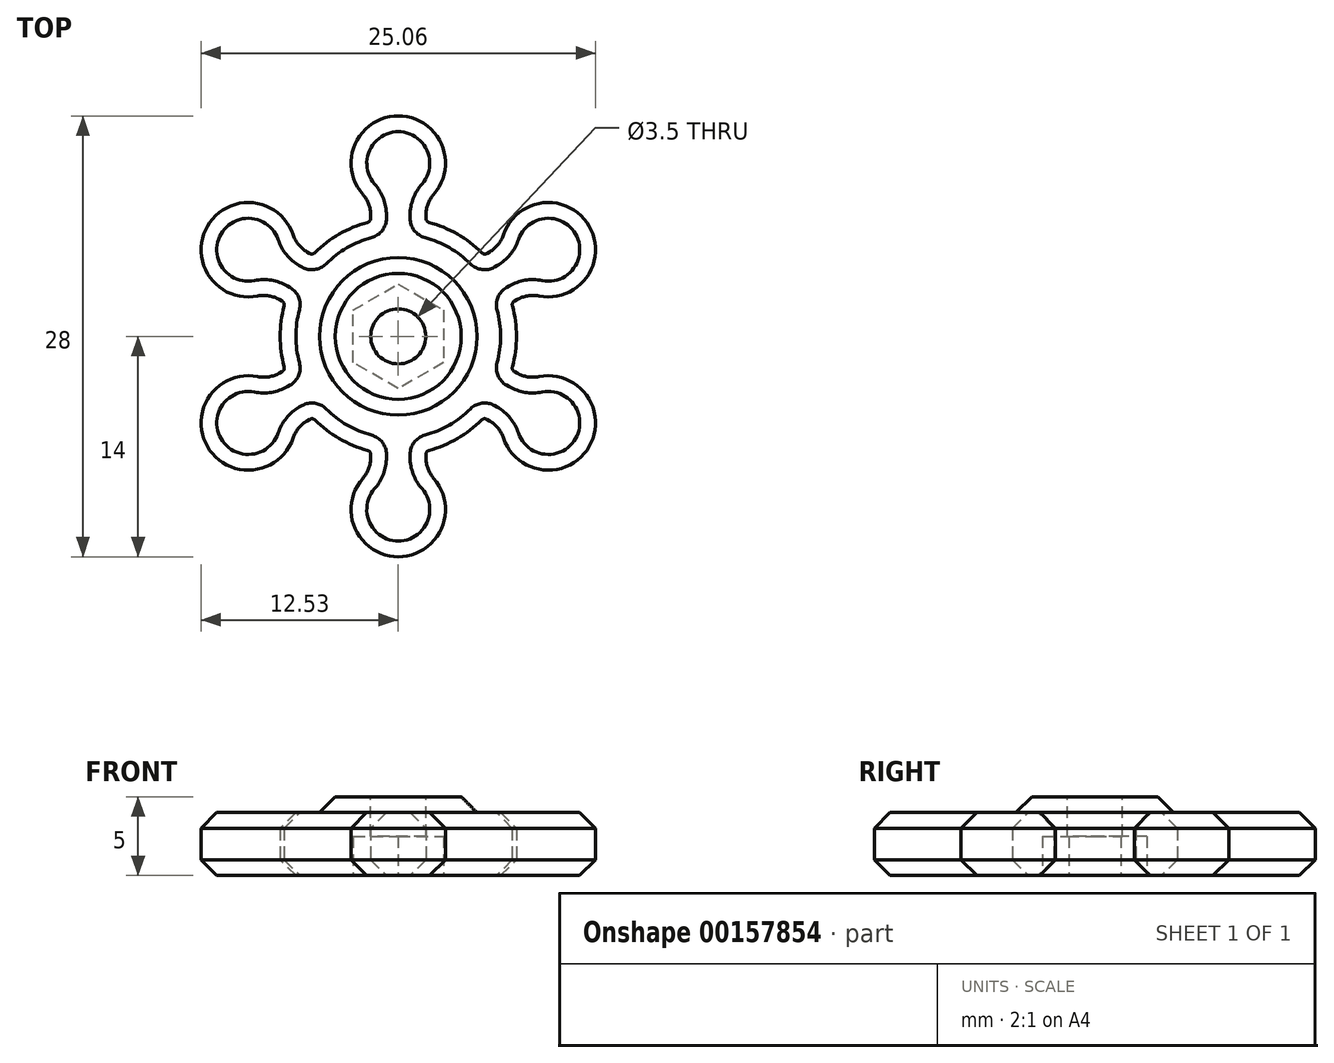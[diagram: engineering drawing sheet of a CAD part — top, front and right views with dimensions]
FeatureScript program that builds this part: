
annotation { "Feature Type Name" : "Feature", "Feature Type Description" : "" }
export const myFeature = defineFeature(function(context is Context, id is Id, definition is map)
    precondition{}
    {
        {
            var Q0;
            Q0=qCreatedBy(makeId("Top.planeOp"),FACE);
            var sketch = newSketch(context, id + "F0", { "sketchPlane" : qUnion([Q0])});
            skArc(sketch, "E0", {"start": v(-1.95, 7.24) * mm, "mid": v(-3.75, 6.5) * mm, "end": v(-5.3, 5.31) * mm});
            skArc(sketch, "E1", {"start": v(2.25, 9.02) * mm, "mid": v(0, 14) * mm, "end": v(-2.25, 9.02) * mm});
            skLineSegment(sketch, "E2.left", {"start": v(-1.75, 7.5) * mm, "end": v(-1.75, 7.7) * mm});
            skLineSegment(sketch, "E2.right", {"start": v(1.75, 7.5) * mm, "end": v(1.75, 7.7) * mm});
            skPoint(sketch, "E3.orphan", {"position": v(-1.75, 0) * mm});
            skPoint(sketch, "E4.visualSharp", {"position": v(-1.75, 8.56) * mm});
            skArc(sketch, "E4.filletArc", {"start": v(-1.75, 7.7) * mm, "mid": v(-1.88, 8.4) * mm, "end": v(-2.25, 9.02) * mm});
            skPoint(sketch, "E5.visualSharp", {"position": v(1.75, 8.56) * mm});
            skArc(sketch, "E5.filletArc", {"start": v(2.25, 9.02) * mm, "mid": v(1.88, 8.4) * mm, "end": v(1.75, 7.7) * mm});
            skPoint(sketch, "E6.visualSharp", {"position": v(1.75, 7.3) * mm});
            skArc(sketch, "E6.filletArc", {"start": v(1.75, 7.5) * mm, "mid": v(1.8, 7.34) * mm, "end": v(1.95, 7.24) * mm});
            skPoint(sketch, "E7.visualSharp", {"position": v(-1.75, 7.3) * mm});
            skArc(sketch, "E7.filletArc", {"start": v(-1.95, 7.24) * mm, "mid": v(-1.8, 7.34) * mm, "end": v(-1.75, 7.5) * mm});
            skArc(sketch, "E8.1.0", {"start": v(-6.68, 6.46) * mm, "mid": v(-12.12, 7) * mm, "end": v(-8.93, 2.56) * mm});
            skArc(sketch, "E8.1.1", {"start": v(-6.68, 6.46) * mm, "mid": v(-6.33, 5.83) * mm, "end": v(-5.79, 5.36) * mm});
            skArc(sketch, "E8.1.2", {"start": v(-7.54, 2.33) * mm, "mid": v(-8.21, 2.57) * mm, "end": v(-8.93, 2.56) * mm});
            skLineSegment(sketch, "E8.1.3", {"start": v(-7.37, 2.24) * mm, "end": v(-7.54, 2.33) * mm});
            skArc(sketch, "E8.1.4", {"start": v(-7.25, 1.93) * mm, "mid": v(-7.26, 2.1) * mm, "end": v(-7.37, 2.24) * mm});
            skLineSegment(sketch, "E8.1.5", {"start": v(-5.62, 5.27) * mm, "end": v(-5.79, 5.36) * mm});
            skArc(sketch, "E8.1.6", {"start": v(-5.62, 5.27) * mm, "mid": v(-5.45, 5.23) * mm, "end": v(-5.3, 5.31) * mm});
            skArc(sketch, "E8.2.0", {"start": v(-8.93, -2.56) * mm, "mid": v(-12.12, -7) * mm, "end": v(-6.68, -6.46) * mm});
            skArc(sketch, "E8.2.1", {"start": v(-8.93, -2.56) * mm, "mid": v(-8.21, -2.57) * mm, "end": v(-7.54, -2.33) * mm});
            skArc(sketch, "E8.2.2", {"start": v(-5.79, -5.36) * mm, "mid": v(-6.33, -5.83) * mm, "end": v(-6.68, -6.46) * mm});
            skLineSegment(sketch, "E8.2.3", {"start": v(-5.62, -5.27) * mm, "end": v(-5.79, -5.36) * mm});
            skArc(sketch, "E8.2.4", {"start": v(-5.3, -5.31) * mm, "mid": v(-5.45, -5.23) * mm, "end": v(-5.62, -5.27) * mm});
            skLineSegment(sketch, "E8.2.5", {"start": v(-7.37, -2.24) * mm, "end": v(-7.54, -2.33) * mm});
            skArc(sketch, "E8.2.6", {"start": v(-7.37, -2.24) * mm, "mid": v(-7.26, -2.1) * mm, "end": v(-7.25, -1.93) * mm});
            skArc(sketch, "E8.3.0", {"start": v(-2.25, -9.02) * mm, "mid": v(0, -14) * mm, "end": v(2.25, -9.02) * mm});
            skArc(sketch, "E8.3.1", {"start": v(-2.25, -9.02) * mm, "mid": v(-1.88, -8.4) * mm, "end": v(-1.75, -7.7) * mm});
            skArc(sketch, "E8.3.2", {"start": v(1.75, -7.7) * mm, "mid": v(1.88, -8.4) * mm, "end": v(2.25, -9.02) * mm});
            skLineSegment(sketch, "E8.3.3", {"start": v(1.75, -7.5) * mm, "end": v(1.75, -7.7) * mm});
            skArc(sketch, "E8.3.4", {"start": v(1.95, -7.24) * mm, "mid": v(1.8, -7.34) * mm, "end": v(1.75, -7.5) * mm});
            skLineSegment(sketch, "E8.3.5", {"start": v(-1.75, -7.5) * mm, "end": v(-1.75, -7.7) * mm});
            skArc(sketch, "E8.3.6", {"start": v(-1.75, -7.5) * mm, "mid": v(-1.8, -7.34) * mm, "end": v(-1.95, -7.24) * mm});
            skArc(sketch, "E8.4.0", {"start": v(6.68, -6.46) * mm, "mid": v(12.12, -7) * mm, "end": v(8.93, -2.56) * mm});
            skArc(sketch, "E8.4.1", {"start": v(6.68, -6.46) * mm, "mid": v(6.33, -5.83) * mm, "end": v(5.79, -5.36) * mm});
            skArc(sketch, "E8.4.2", {"start": v(7.54, -2.33) * mm, "mid": v(8.21, -2.57) * mm, "end": v(8.93, -2.56) * mm});
            skLineSegment(sketch, "E8.4.3", {"start": v(7.37, -2.24) * mm, "end": v(7.54, -2.33) * mm});
            skArc(sketch, "E8.4.4", {"start": v(7.25, -1.93) * mm, "mid": v(7.26, -2.1) * mm, "end": v(7.37, -2.24) * mm});
            skLineSegment(sketch, "E8.4.5", {"start": v(5.62, -5.27) * mm, "end": v(5.79, -5.36) * mm});
            skArc(sketch, "E8.4.6", {"start": v(5.62, -5.27) * mm, "mid": v(5.45, -5.23) * mm, "end": v(5.3, -5.31) * mm});
            skArc(sketch, "E8.5.0", {"start": v(8.93, 2.56) * mm, "mid": v(12.12, 7) * mm, "end": v(6.68, 6.46) * mm});
            skArc(sketch, "E8.5.1", {"start": v(8.93, 2.56) * mm, "mid": v(8.21, 2.57) * mm, "end": v(7.54, 2.33) * mm});
            skArc(sketch, "E8.5.2", {"start": v(5.79, 5.36) * mm, "mid": v(6.33, 5.83) * mm, "end": v(6.68, 6.46) * mm});
            skLineSegment(sketch, "E8.5.3", {"start": v(5.62, 5.27) * mm, "end": v(5.79, 5.36) * mm});
            skArc(sketch, "E8.5.4", {"start": v(5.3, 5.31) * mm, "mid": v(5.45, 5.23) * mm, "end": v(5.62, 5.27) * mm});
            skLineSegment(sketch, "E8.5.5", {"start": v(7.37, 2.24) * mm, "end": v(7.54, 2.33) * mm});
            skArc(sketch, "E8.5.6", {"start": v(7.37, 2.24) * mm, "mid": v(7.26, 2.1) * mm, "end": v(7.25, 1.93) * mm});
            skArc(sketch, "E9.trimOffspring", {"start": v(-7.25, 1.93) * mm, "mid": v(-7.5, 0) * mm, "end": v(-7.25, -1.93) * mm});
            skArc(sketch, "E10.trimOffspring", {"start": v(-5.3, -5.31) * mm, "mid": v(-3.75, -6.5) * mm, "end": v(-1.95, -7.24) * mm});
            skArc(sketch, "E11.trimOffspring", {"start": v(1.95, -7.24) * mm, "mid": v(3.75, -6.5) * mm, "end": v(5.3, -5.31) * mm});
            skArc(sketch, "E12.trimOffspring", {"start": v(7.25, -1.93) * mm, "mid": v(7.5, 0) * mm, "end": v(7.25, 1.93) * mm});
            skArc(sketch, "E13.trimOffspring", {"start": v(5.3, 5.31) * mm, "mid": v(3.75, 6.5) * mm, "end": v(1.95, 7.24) * mm});
            skSolve(sketch);
        }
        {
            var Q0;
            Q0 = qSketchRegion(id + "F0", true);
            extrude(context, id + "F1", {"entities" : qUnion([Q0]), "depth" : 4 * mm});
        }
        {
            var Q0;
            Q0=qCreatedBy(makeId("Top.planeOp"),FACE);
            var sketch = newSketch(context, id + "F2", { "sketchPlane" : qUnion([Q0])});
            skCircle(sketch, "E14.cCircle", {"center": v(0, 0) * mm, "radius": 2.88 * mm, "construction": true});
            skLineSegment(sketch, "E14.0", {"start": v(2.88, 1.66) * mm, "end": v(2.88, -1.66) * mm});
            skLineSegment(sketch, "E14.1", {"start": v(2.88, -1.66) * mm, "end": v(0, -3.32) * mm});
            skLineSegment(sketch, "E14.2", {"start": v(0, -3.32) * mm, "end": v(-2.87, -1.66) * mm});
            skLineSegment(sketch, "E14.3", {"start": v(-2.87, -1.66) * mm, "end": v(-2.88, 1.66) * mm});
            skLineSegment(sketch, "E14.4", {"start": v(-2.88, 1.66) * mm, "end": v(0, 3.32) * mm});
            skLineSegment(sketch, "E14.5", {"start": v(0, 3.32) * mm, "end": v(2.88, 1.66) * mm});
            skPoint(sketch, "E14.0.midPoint", {"position": v(2.88, 0) * mm});
            skSolve(sketch);
        }
        {
            var Q0;
            Q0=makeQuery(id+"F2.imprint","IMPRINT",FACE,{"disambiguationData":[TD([[makeQuery(id+"F2.imprint","IMPRINT",EDGE,{"derivedFrom":sQuery(id+"F2.wireOp",EDGE,"E14.0")}),-1.0]])]});
            extrude(context, id + "F3", {"entities" : qUnion([Q0]), "operationType" : NewBodyOperationType.REMOVE, "depth" : 2.5 * mm});
        }
        {
            var Q0;
            Q0=makeQuery(id+"F1.opExtrude","CAP_FACE",FACE,{"disambiguationData":[OSD([sQuery(id+"F0.wireOp",EDGE,"E0"),sQuery(id+"F0.wireOp",EDGE,"tknGAK8U-p5LG-1uRe-C4Xr-DTzWjZsoBAFM"),sQuery(id+"F0.wireOp",EDGE,"E1"),sQuery(id+"F0.wireOp",EDGE,"E2.left"),sQuery(id+"F0.wireOp",EDGE,"E2.right"),sQuery(id+"F0.wireOp",EDGE,"E4.filletArc"),sQuery(id+"F0.wireOp",EDGE,"E5.filletArc"),sQuery(id+"F0.wireOp",EDGE,"E6.filletArc"),sQuery(id+"F0.wireOp",EDGE,"E7.filletArc"),sQuery(id+"F0.wireOp",EDGE,"E8.1.0"),sQuery(id+"F0.wireOp",EDGE,"E8.1.1"),sQuery(id+"F0.wireOp",EDGE,"E8.1.2"),sQuery(id+"F0.wireOp",EDGE,"E8.1.3"),sQuery(id+"F0.wireOp",EDGE,"E8.1.4"),sQuery(id+"F0.wireOp",EDGE,"E8.1.5"),sQuery(id+"F0.wireOp",EDGE,"E8.1.6"),sQuery(id+"F0.wireOp",EDGE,"E8.2.0"),sQuery(id+"F0.wireOp",EDGE,"E8.2.1"),sQuery(id+"F0.wireOp",EDGE,"E8.2.2"),sQuery(id+"F0.wireOp",EDGE,"E8.2.3"),sQuery(id+"F0.wireOp",EDGE,"E8.2.4"),sQuery(id+"F0.wireOp",EDGE,"E8.2.5"),sQuery(id+"F0.wireOp",EDGE,"E8.2.6"),sQuery(id+"F0.wireOp",EDGE,"E8.3.0"),sQuery(id+"F0.wireOp",EDGE,"E8.3.1"),sQuery(id+"F0.wireOp",EDGE,"E8.3.2"),sQuery(id+"F0.wireOp",EDGE,"E8.3.3"),sQuery(id+"F0.wireOp",EDGE,"E8.3.4"),sQuery(id+"F0.wireOp",EDGE,"E8.3.5"),sQuery(id+"F0.wireOp",EDGE,"E8.3.6"),sQuery(id+"F0.wireOp",EDGE,"E8.4.0"),sQuery(id+"F0.wireOp",EDGE,"E8.4.1"),sQuery(id+"F0.wireOp",EDGE,"E8.4.2"),sQuery(id+"F0.wireOp",EDGE,"E8.4.3"),sQuery(id+"F0.wireOp",EDGE,"E8.4.4"),sQuery(id+"F0.wireOp",EDGE,"E8.4.5"),sQuery(id+"F0.wireOp",EDGE,"E8.4.6"),sQuery(id+"F0.wireOp",EDGE,"E8.5.0"),sQuery(id+"F0.wireOp",EDGE,"E8.5.1"),sQuery(id+"F0.wireOp",EDGE,"E8.5.2"),sQuery(id+"F0.wireOp",EDGE,"E8.5.3"),sQuery(id+"F0.wireOp",EDGE,"E8.5.4"),sQuery(id+"F0.wireOp",EDGE,"E8.5.5"),sQuery(id+"F0.wireOp",EDGE,"E8.5.6"),sQuery(id+"F0.wireOp",EDGE,"E9.trimOffspring"),sQuery(id+"F0.wireOp",EDGE,"E10.trimOffspring"),sQuery(id+"F0.wireOp",EDGE,"E11.trimOffspring"),sQuery(id+"F0.wireOp",EDGE,"E12.trimOffspring"),sQuery(id+"F0.wireOp",EDGE,"E13.trimOffspring")])],"isStart":false});
            var sketch = newSketch(context, id + "F4", { "sketchPlane" : qUnion([Q0])});
            skCircle(sketch, "E15", {"center": v(0, 0) * mm, "radius": 4 * mm});
            skSolve(sketch);
        }
        {
            var Q0;
            Q0 = qSketchRegion(id + "F4", true);
            extrude(context, id + "F5", {"entities" : qUnion([Q0]), "operationType" : NewBodyOperationType.ADD, "depth" : 1 * mm});
        }
        {
            var Q0;
            Q0=makeQuery(id+"F5.opExtrude","CAP_FACE",FACE,{"disambiguationData":[OSD([sQuery(id+"F4.wireOp",EDGE,"E15")])],"isStart":false});
            var sketch = newSketch(context, id + "F6", { "sketchPlane" : qUnion([Q0])});
            skCircle(sketch, "E16", {"center": v(0, 0) * mm, "radius": 1.75 * mm});
            skSolve(sketch);
        }
        {
            var Q0;
            Q0 = qSketchRegion(id + "F6", true);
            extrude(context, id + "F7", {"entities" : qUnion([Q0]), "operationType" : NewBodyOperationType.REMOVE, "endBound" : BoundingType.THROUGH_ALL, "oppositeDirection" : true, "depth" : 25 * mm});
        }
        {
            var Q0;
            Q0=makeQuery(id+"F1.opExtrude","CAP_FACE",FACE,{"disambiguationData":[OSD([sQuery(id+"F0.wireOp",EDGE,"E0"),sQuery(id+"F0.wireOp",EDGE,"E1"),sQuery(id+"F0.wireOp",EDGE,"E2.left"),sQuery(id+"F0.wireOp",EDGE,"E2.right"),sQuery(id+"F0.wireOp",EDGE,"E4.filletArc"),sQuery(id+"F0.wireOp",EDGE,"E5.filletArc"),sQuery(id+"F0.wireOp",EDGE,"E6.filletArc"),sQuery(id+"F0.wireOp",EDGE,"E7.filletArc"),sQuery(id+"F0.wireOp",EDGE,"E8.1.0"),sQuery(id+"F0.wireOp",EDGE,"E8.1.1"),sQuery(id+"F0.wireOp",EDGE,"E8.1.2"),sQuery(id+"F0.wireOp",EDGE,"E8.1.3"),sQuery(id+"F0.wireOp",EDGE,"E8.1.4"),sQuery(id+"F0.wireOp",EDGE,"E8.1.5"),sQuery(id+"F0.wireOp",EDGE,"E8.1.6"),sQuery(id+"F0.wireOp",EDGE,"E8.2.0"),sQuery(id+"F0.wireOp",EDGE,"E8.2.1"),sQuery(id+"F0.wireOp",EDGE,"E8.2.2"),sQuery(id+"F0.wireOp",EDGE,"E8.2.3"),sQuery(id+"F0.wireOp",EDGE,"E8.2.4"),sQuery(id+"F0.wireOp",EDGE,"E8.2.5"),sQuery(id+"F0.wireOp",EDGE,"E8.2.6"),sQuery(id+"F0.wireOp",EDGE,"E8.3.0"),sQuery(id+"F0.wireOp",EDGE,"E8.3.1"),sQuery(id+"F0.wireOp",EDGE,"E8.3.2"),sQuery(id+"F0.wireOp",EDGE,"E8.3.3"),sQuery(id+"F0.wireOp",EDGE,"E8.3.4"),sQuery(id+"F0.wireOp",EDGE,"E8.3.5"),sQuery(id+"F0.wireOp",EDGE,"E8.3.6"),sQuery(id+"F0.wireOp",EDGE,"E8.4.0"),sQuery(id+"F0.wireOp",EDGE,"E8.4.1"),sQuery(id+"F0.wireOp",EDGE,"E8.4.2"),sQuery(id+"F0.wireOp",EDGE,"E8.4.3"),sQuery(id+"F0.wireOp",EDGE,"E8.4.4"),sQuery(id+"F0.wireOp",EDGE,"E8.4.5"),sQuery(id+"F0.wireOp",EDGE,"E8.4.6"),sQuery(id+"F0.wireOp",EDGE,"E8.5.0"),sQuery(id+"F0.wireOp",EDGE,"E8.5.1"),sQuery(id+"F0.wireOp",EDGE,"E8.5.2"),sQuery(id+"F0.wireOp",EDGE,"E8.5.3"),sQuery(id+"F0.wireOp",EDGE,"E8.5.4"),sQuery(id+"F0.wireOp",EDGE,"E8.5.5"),sQuery(id+"F0.wireOp",EDGE,"E8.5.6"),sQuery(id+"F0.wireOp",EDGE,"E9.trimOffspring"),sQuery(id+"F0.wireOp",EDGE,"E10.trimOffspring"),sQuery(id+"F0.wireOp",EDGE,"E11.trimOffspring"),sQuery(id+"F0.wireOp",EDGE,"E12.trimOffspring"),sQuery(id+"F0.wireOp",EDGE,"E13.trimOffspring")])],"isStart":false});
            var Q1;
            Q1=makeQuery(id+"F1.opExtrude","CAP_EDGE",EDGE,{"disambiguationData":[OSD([sQuery(id+"F0.wireOp",EDGE,"E8.2.0")])],"isStart":true});
            chamfer(context, id + "F8", {"entities" : qUnion([Q0, Q1]), "width" : 1 * mm, "tangentPropagation" : true});
        }
    });
